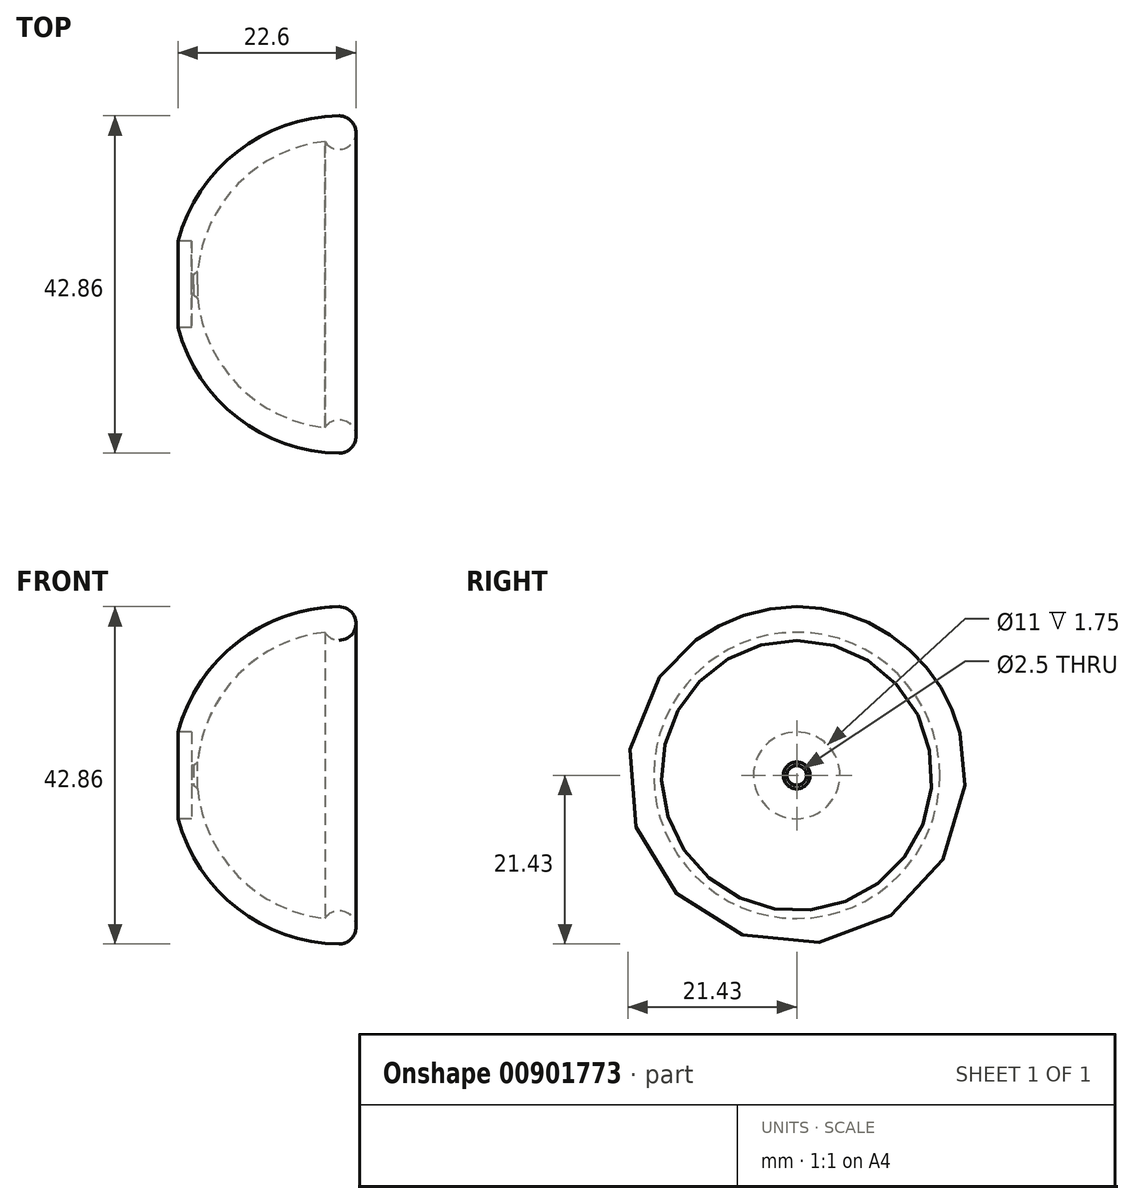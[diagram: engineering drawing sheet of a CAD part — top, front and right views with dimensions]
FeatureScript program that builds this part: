
annotation { "Feature Type Name" : "Feature", "Feature Type Description" : "" }
export const myFeature = defineFeature(function(context is Context, id is Id, definition is map)
    precondition{}
    {
        {
            var Q0;
            Q0=qCreatedBy(makeId("Front.planeOp"),FACE);
            var sketch = newSketch(context, id + "F0", { "sketchPlane" : qUnion([Q0])});
            skLineSegment(sketch, "E0", {"start": v(0, 5.5) * mm, "end": v(0, 0) * mm});
            skLineSegment(sketch, "E1", {"start": v(0, 5.5) * mm, "end": v(-1.75, 5.5) * mm});
            skLineSegment(sketch, "E2", {"start": v(0, 0) * mm, "end": v(0.67, 0) * mm});
            skArc(sketch, "E3", {"start": v(16.9, 18.18) * mm, "mid": v(5.32, 12.19) * mm, "end": v(0.67, 0) * mm});
            skArc(sketch, "E4", {"start": v(18.7, 21.43) * mm, "mid": v(5.8, 16.9) * mm, "end": v(-1.75, 5.5) * mm});
            skCircle(sketch, "E5", {"center": v(18.72, 19.3) * mm, "radius": 2.13 * mm});
            skSolve(sketch);
        }
        {
            var Q0;
            {var subQ0=sQuery(id+"F0.wireOp",EDGE,"E5");var subQ1=makeQuery(id+"F0.imprint","INTERSECT",VERTEX,{"derivedFrom":[sQuery(id+"F0.wireOp",EDGE,"E3"),subQ0]});Q0=makeQuery(id+"F0.imprint","IMPRINT",FACE,{"disambiguationData":[TD([[makeQuery(id+"F0.imprint","IMPRINT",EDGE,{"disambiguationData":[TD([[subQ1,1.0]])],"derivedFrom":subQ0}),1.0]])]});}
            var Q1;
            {var subQ2=sQuery(id+"F0.wireOp",EDGE,"E0");Q1=makeQuery(id+"F0.imprint","IMPRINT",FACE,{"disambiguationData":[TD([[makeQuery(id+"F0.imprint","IMPRINT",EDGE,{"derivedFrom":subQ2}),1.0]])]});}
            var Q2;
            Q2=sQuery(id+"F0.wireOp",EDGE,"E2");
            revolve(context, id + "F1", {"surfaceOperationType" : NewSurfaceOperationType.NEW, "entities" : qUnion([Q0, Q1]), "axis" : qUnion([Q2]), "revolveType" : RevolveType.FULL});
        }
        {
            var Q0;
            Q0=makeQuery(id+"F1.opRevolve","SWEPT_FACE",FACE,{"disambiguationData":[OSD([sQuery(id+"F0.wireOp",EDGE,"E0")])]});
            var sketch = newSketch(context, id + "F2", { "sketchPlane" : qUnion([Q0])});
            skCircle(sketch, "E6", {"center": v(0, 0) * mm, "radius": 1.25 * mm});
            skCircle(sketch, "E7.0", {"center": v(0, 0) * mm, "radius": 21.43 * mm});
            skSolve(sketch);
        }
        {
            var Q0;
            Q0=makeQuery(id+"F2.imprint","IMPRINT",FACE,{"disambiguationData":[TD([[makeQuery(id+"F2.imprint","IMPRINT",EDGE,{"derivedFrom":sQuery(id+"F2.wireOp",EDGE,"E6")}),1.0]])]});
            var Q1;
            Q1=sQuery(id+"F2.wireOp",EDGE,"E6");
            extrude(context, id + "F3", {"entities" : qUnion([Q0]), "operationType" : NewBodyOperationType.REMOVE, "surfaceEntities" : qUnion([Q1]), "endBound" : BoundingType.THROUGH_ALL, "oppositeDirection" : true, "depth" : 25 * mm, "offsetDistance" : 25 * mm});
        }
        {
            var Q0;
            Q0=makeQuery(id+"F3.boolean.opBoolean","INTERSECT",EDGE,{"derivedFrom":[makeQuery(id+"F1.opRevolve","SWEPT_FACE",FACE,{"disambiguationData":[OSD([sQuery(id+"F0.wireOp",EDGE,"E3")])]}),makeQuery(id+"F3.opExtrude","SWEPT_FACE",FACE,{"disambiguationData":[OSD([sQuery(id+"F2.wireOp",EDGE,"E6")])]})]});
            chamfer(context, id + "F4", {"entities" : qUnion([Q0]), "width" : .5 * mm, "tangentPropagation" : true});
        }
    });
